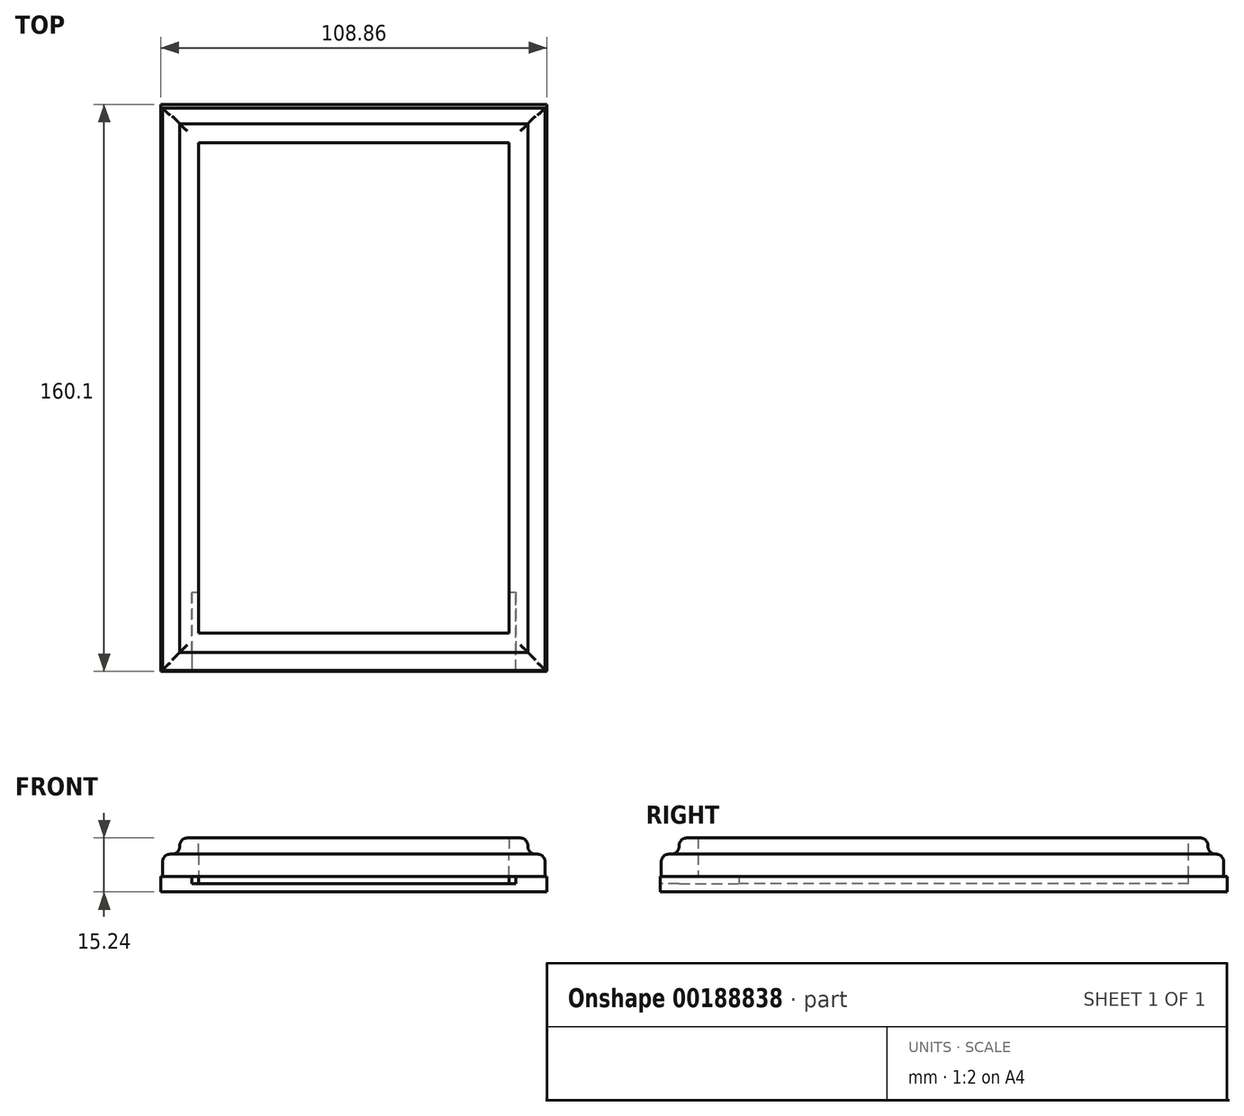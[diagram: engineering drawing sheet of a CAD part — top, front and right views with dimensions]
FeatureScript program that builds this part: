
annotation { "Feature Type Name" : "Feature", "Feature Type Description" : "" }
export const myFeature = defineFeature(function(context is Context, id is Id, definition is map)
    precondition{}
    {
        {
            var Q0;
            Q0=qCreatedBy(makeId("Top.planeOp"),FACE);
            var sketch = newSketch(context, id + "F0", { "sketchPlane" : qUnion([Q0])});
            skLineSegment(sketch, "E0.bottom", {"start": v(-90.68, 102.35) * mm, "end": v(17.27, 102.35) * mm});
            skLineSegment(sketch, "E0.top", {"start": v(-90.68, -56.4) * mm, "end": v(17.27, -56.4) * mm});
            skLineSegment(sketch, "E0.left", {"start": v(-90.68, 102.35) * mm, "end": v(-90.68, -56.4) * mm});
            skLineSegment(sketch, "E0.right", {"start": v(17.27, 102.35) * mm, "end": v(17.27, -56.4) * mm});
            skLineSegment(sketch, "E1.bottom", {"start": v(-90.68, 102.35) * mm, "end": v(-82.04, 102.35) * mm});
            skLineSegment(sketch, "E1.left", {"start": v(-90.68, 102.35) * mm, "end": v(-90.68, 93.72) * mm});
            skLineSegment(sketch, "E2.bottom", {"start": v(17.27, 102.35) * mm, "end": v(8.64, 102.35) * mm});
            skLineSegment(sketch, "E2.left", {"start": v(17.27, 102.35) * mm, "end": v(17.27, 93.72) * mm});
            skLineSegment(sketch, "E3.bottom", {"start": v(-90.68, -56.4) * mm, "end": v(-82.04, -56.4) * mm});
            skLineSegment(sketch, "E3.left", {"start": v(-90.68, -56.4) * mm, "end": v(-90.68, -47.76) * mm});
            skLineSegment(sketch, "E4.bottom", {"start": v(17.27, -56.4) * mm, "end": v(8.64, -56.4) * mm});
            skLineSegment(sketch, "E4.left", {"start": v(17.27, -56.4) * mm, "end": v(17.27, -47.76) * mm});
            skLineSegment(sketch, "E5.bottom", {"start": v(-80.54, 92.48) * mm, "end": v(7.1, 92.48) * mm});
            skLineSegment(sketch, "E5.top", {"start": v(-80.54, -45.95) * mm, "end": v(7.1, -45.95) * mm});
            skLineSegment(sketch, "E5.left", {"start": v(-80.54, 92.48) * mm, "end": v(-80.54, -45.95) * mm});
            skLineSegment(sketch, "E5.right", {"start": v(7.1, 92.48) * mm, "end": v(7.1, -45.95) * mm});
            skPoint(sketch, "E3.right.end.orphan", {"position": v(-80.54, -45.95) * mm});
            skSolve(sketch);
        }
        {
            var Q0;
            Q0 = qSketchRegion(id + "F0", true);
            extrude(context, id + "F1", {"entities" : qUnion([Q0]), "depth" : 6.35 * mm});
        }
        {
            var Q0;
            Q0=qCreatedBy(makeId("Top.planeOp"),FACE);
            var sketch = newSketch(context, id + "F2", { "sketchPlane" : qUnion([Q0])});
            skLineSegment(sketch, "E6.bottom", {"start": v(-91.13, -56.74) * mm, "end": v(-82.42, -56.74) * mm});
            skLineSegment(sketch, "E6.top", {"start": v(-91.13, 103.36) * mm, "end": v(17.73, 103.36) * mm});
            skLineSegment(sketch, "E6.left", {"start": v(-91.13, -56.74) * mm, "end": v(-91.13, 103.36) * mm});
            skLineSegment(sketch, "E6.right", {"start": v(17.73, -56.74) * mm, "end": v(17.73, 103.36) * mm});
            skLineSegment(sketch, "E7.top", {"start": v(-82.42, 94.23) * mm, "end": v(9.02, 94.23) * mm});
            skLineSegment(sketch, "E7.left", {"start": v(-82.42, -48.01) * mm, "end": v(-82.42, 94.23) * mm});
            skLineSegment(sketch, "E7.right", {"start": v(9.02, -48.01) * mm, "end": v(9.02, 94.23) * mm});
            skLineSegment(sketch, "E8", {"start": v(44.34, -69.5) * mm, "end": v(109.88, 53.73) * mm});
            skLineSegment(sketch, "E9", {"start": v(9.02, -48.01) * mm, "end": v(9.02, -56.74) * mm});
            skLineSegment(sketch, "E10", {"start": v(9.02, -56.74) * mm, "end": v(9.02, -48.01) * mm});
            skLineSegment(sketch, "E11", {"start": v(-82.42, -48.01) * mm, "end": v(-82.42, -56.74) * mm});
            skLineSegment(sketch, "E12", {"start": v(-82.42, -56.74) * mm, "end": v(-82.42, -48.01) * mm});
            skLineSegment(sketch, "E13.trimOffspring", {"start": v(9.02, -56.74) * mm, "end": v(17.73, -56.74) * mm});
            skSolve(sketch);
        }
        {
            var Q0;
            Q0=makeQuery(id+"F2.imprint","IMPRINT",FACE,{"disambiguationData":[TD([[makeQuery(id+"F2.imprint","IMPRINT",EDGE,{"derivedFrom":sQuery(id+"F2.wireOp",EDGE,"E6.bottom")}),1.0]])]});
            extrude(context, id + "F3", {"entities" : qUnion([Q0]), "operationType" : NewBodyOperationType.ADD, "oppositeDirection" : true, "depth" : 2.03 * mm});
        }
        {
            var Q0;
            Q0=qCreatedBy(makeId("Top.planeOp"),FACE);
            cPlane(context, id + "F4", {"entities" : qUnion([Q0]), "cplaneType" : CPlaneType.OFFSET, "offset" : 2.03 * mm, "oppositeDirection" : true, "width" : 152.4 * mm, "height" : 152.4 * mm});
        }
        {
            var Q0;
            Q0=qCreatedBy(id+"F4.planeOp",FACE);
            var sketch = newSketch(context, id + "F5", { "sketchPlane" : qUnion([Q0])});
            skLineSegment(sketch, "E14.bottom", {"start": v(-91.13, -56.74) * mm, "end": v(17.73, -56.74) * mm});
            skLineSegment(sketch, "E14.top", {"start": v(-91.13, 103.36) * mm, "end": v(17.73, 103.36) * mm});
            skLineSegment(sketch, "E14.left", {"start": v(-91.13, -56.74) * mm, "end": v(-91.13, 103.36) * mm});
            skLineSegment(sketch, "E14.right", {"start": v(17.73, -56.74) * mm, "end": v(17.73, 103.36) * mm});
            skSolve(sketch);
        }
        {
            var Q0;
            Q0 = qSketchRegion(id + "F5", true);
            extrude(context, id + "F6", {"entities" : qUnion([Q0]), "operationType" : NewBodyOperationType.ADD, "oppositeDirection" : true, "depth" : 2.3 * mm});
        }
        {
            var Q0;
            Q0=qCreatedBy(makeId("Top.planeOp"),FACE);
            var sketch = newSketch(context, id + "F7", { "sketchPlane" : qUnion([Q0])});
            skLineSegment(sketch, "E15.bottom", {"start": v(-80.54, 92.48) * mm, "end": v(7.1, 92.48) * mm});
            skLineSegment(sketch, "E15.top", {"start": v(-80.54, -45.95) * mm, "end": v(7.1, -45.95) * mm});
            skLineSegment(sketch, "E15.left", {"start": v(-80.54, 92.48) * mm, "end": v(-80.54, -45.95) * mm});
            skLineSegment(sketch, "E15.right", {"start": v(7.1, 92.48) * mm, "end": v(7.1, -45.95) * mm});
            skLineSegment(sketch, "E16.left", {"start": v(7.1, -45.95) * mm, "end": v(7.1, -51.34) * mm});
            skPoint(sketch, "E17.firstSnap0", {"position": v(-85.84, 92.48) * mm});
            skPoint(sketch, "E17.firstSnap1", {"position": v(-80.54, 97.92) * mm});
            skPoint(sketch, "E17.oppositeSnap0", {"position": v(17.73, -51.34) * mm});
            skPoint(sketch, "E17.oppositeSnap1", {"position": v(12.41, -45.95) * mm});
            skLineSegment(sketch, "E17.bottom", {"start": v(-85.84, 97.92) * mm, "end": v(12.41, 97.92) * mm});
            skLineSegment(sketch, "E17.top", {"start": v(-85.84, -51.34) * mm, "end": v(12.41, -51.34) * mm});
            skLineSegment(sketch, "E17.left", {"start": v(-85.84, 97.92) * mm, "end": v(-85.84, -51.34) * mm});
            skLineSegment(sketch, "E17.right", {"start": v(12.41, 97.92) * mm, "end": v(12.41, -51.34) * mm});
            skPoint(sketch, "E18.orphan", {"position": v(17.73, -56.74) * mm});
            skPoint(sketch, "E16.right.start.orphan", {"position": v(17.73, -45.95) * mm});
            skPoint(sketch, "E19.top.start.orphan", {"position": v(-80.54, 103.36) * mm});
            skPoint(sketch, "E19.right.start.orphan", {"position": v(-91.13, 92.48) * mm});
            skSolve(sketch);
        }
        {
            var Q0;
            Q0 = qSketchRegion(id + "F7", true);
            extrude(context, id + "F8", {"entities" : qUnion([Q0]), "operationType" : NewBodyOperationType.ADD, "oppositeDirection" : true, "depth" : 4.2 * mm});
        }
        {
            var Q0;
            Q0=qCreatedBy(makeId("Top.planeOp"),FACE);
            var sketch = newSketch(context, id + "F9", { "sketchPlane" : qUnion([Q0])});
            skLineSegment(sketch, "E20.bottom", {"start": v(-80.54, 92.48) * mm, "end": v(7.1, 92.48) * mm});
            skLineSegment(sketch, "E20.top", {"start": v(-80.54, -45.95) * mm, "end": v(7.1, -45.95) * mm});
            skLineSegment(sketch, "E20.left", {"start": v(-80.54, 92.48) * mm, "end": v(-80.54, -45.95) * mm});
            skLineSegment(sketch, "E20.right", {"start": v(7.1, 92.48) * mm, "end": v(7.1, -45.95) * mm});
            skPoint(sketch, "E21.firstSnap0", {"position": v(-85.83, 103.35) * mm});
            skPoint(sketch, "E21.firstSnap1", {"position": v(-91.12, 97.91) * mm});
            skPoint(sketch, "E21.oppositeSnap0", {"position": v(7.1, -51.37) * mm});
            skPoint(sketch, "E21.oppositeSnap1", {"position": v(12.43, -45.95) * mm});
            skLineSegment(sketch, "E21.bottom", {"start": v(-85.83, 97.91) * mm, "end": v(12.43, 97.91) * mm});
            skLineSegment(sketch, "E21.top", {"start": v(-85.83, -51.37) * mm, "end": v(12.43, -51.37) * mm});
            skLineSegment(sketch, "E21.left", {"start": v(-85.83, 97.91) * mm, "end": v(-85.83, -51.37) * mm});
            skLineSegment(sketch, "E21.right", {"start": v(12.43, 97.91) * mm, "end": v(12.43, -51.37) * mm});
            skPoint(sketch, "E22.right.start.orphan", {"position": v(17.78, -45.95) * mm});
            skPoint(sketch, "E22.top.start.orphan", {"position": v(7.1, -56.78) * mm});
            skPoint(sketch, "E23.orphan", {"position": v(-91.12, 92.48) * mm});
            skPoint(sketch, "E24.orphan", {"position": v(-91.12, 103.35) * mm});
            skPoint(sketch, "E25.left.end.orphan", {"position": v(-80.54, 103.35) * mm});
            skSolve(sketch);
        }
        {
            var Q0;
            Q0 = qSketchRegion(id + "F9", true);
            extrude(context, id + "F10", {"entities" : qUnion([Q0]), "operationType" : NewBodyOperationType.ADD, "depth" : 10.92 * mm});
        }
        {
            var Q0;
            Q0=makeQuery(id+"F10.opExtrude","CAP_EDGE",EDGE,{"disambiguationData":[OSD([sQuery(id+"F9.wireOp",EDGE,"E21.right")])],"isStart":false});
            var Q1;
            Q1=makeQuery(id+"F10.boolean.opBoolean","INTERSECT",EDGE,{"derivedFrom":[makeQuery(id+"F1.opExtrude","CAP_FACE",FACE,{"disambiguationData":[OSD([sQuery(id+"F0.wireOp",EDGE,"E0.bottom"),sQuery(id+"F0.wireOp",EDGE,"E0.top"),sQuery(id+"F0.wireOp",EDGE,"E0.left"),sQuery(id+"F0.wireOp",EDGE,"E0.right"),sQuery(id+"F0.wireOp",EDGE,"E1.bottom"),sQuery(id+"F0.wireOp",EDGE,"E1.left"),sQuery(id+"F0.wireOp",EDGE,"E2.bottom"),sQuery(id+"F0.wireOp",EDGE,"E2.left"),sQuery(id+"F0.wireOp",EDGE,"E3.bottom"),sQuery(id+"F0.wireOp",EDGE,"E3.left"),sQuery(id+"F0.wireOp",EDGE,"E4.bottom"),sQuery(id+"F0.wireOp",EDGE,"E4.left"),sQuery(id+"F0.wireOp",EDGE,"E5.bottom"),sQuery(id+"F0.wireOp",EDGE,"E5.top"),sQuery(id+"F0.wireOp",EDGE,"E5.left"),sQuery(id+"F0.wireOp",EDGE,"E5.right")])],"isStart":false}),makeQuery(id+"F10.opExtrude","SWEPT_FACE",FACE,{"disambiguationData":[OSD([sQuery(id+"F9.wireOp",EDGE,"E21.right")])]})]});
            var Q2;
            Q2=makeQuery(id+"F1.opExtrude","CAP_EDGE",EDGE,{"disambiguationData":[OSD([sQuery(id+"F0.wireOp",EDGE,"E0.right"),sQuery(id+"F0.wireOp",EDGE,"E2.left"),sQuery(id+"F0.wireOp",EDGE,"E4.left")])],"isStart":false});
            var Q3;
            Q3=makeQuery(id+"F10.opExtrude","CAP_EDGE",EDGE,{"disambiguationData":[OSD([sQuery(id+"F9.wireOp",EDGE,"E21.bottom")])],"isStart":false});
            var Q4;
            Q4=makeQuery(id+"F10.boolean.opBoolean","INTERSECT",EDGE,{"derivedFrom":[makeQuery(id+"F1.opExtrude","CAP_FACE",FACE,{"disambiguationData":[OSD([sQuery(id+"F0.wireOp",EDGE,"E0.bottom"),sQuery(id+"F0.wireOp",EDGE,"E0.top"),sQuery(id+"F0.wireOp",EDGE,"E0.left"),sQuery(id+"F0.wireOp",EDGE,"E0.right"),sQuery(id+"F0.wireOp",EDGE,"E1.bottom"),sQuery(id+"F0.wireOp",EDGE,"E1.left"),sQuery(id+"F0.wireOp",EDGE,"E2.bottom"),sQuery(id+"F0.wireOp",EDGE,"E2.left"),sQuery(id+"F0.wireOp",EDGE,"E3.bottom"),sQuery(id+"F0.wireOp",EDGE,"E3.left"),sQuery(id+"F0.wireOp",EDGE,"E4.bottom"),sQuery(id+"F0.wireOp",EDGE,"E4.left"),sQuery(id+"F0.wireOp",EDGE,"E5.bottom"),sQuery(id+"F0.wireOp",EDGE,"E5.top"),sQuery(id+"F0.wireOp",EDGE,"E5.left"),sQuery(id+"F0.wireOp",EDGE,"E5.right")])],"isStart":false}),makeQuery(id+"F10.opExtrude","SWEPT_FACE",FACE,{"disambiguationData":[OSD([sQuery(id+"F9.wireOp",EDGE,"E21.bottom")])]})]});
            var Q5;
            Q5=makeQuery(id+"F1.opExtrude","CAP_EDGE",EDGE,{"disambiguationData":[OSD([sQuery(id+"F0.wireOp",EDGE,"E0.bottom"),sQuery(id+"F0.wireOp",EDGE,"E1.bottom"),sQuery(id+"F0.wireOp",EDGE,"E2.bottom")])],"isStart":false});
            var Q6;
            Q6=makeQuery(id+"F10.opExtrude","CAP_EDGE",EDGE,{"disambiguationData":[OSD([sQuery(id+"F9.wireOp",EDGE,"E21.left")])],"isStart":false});
            var Q7;
            Q7=makeQuery(id+"F1.opExtrude","CAP_EDGE",EDGE,{"disambiguationData":[OSD([sQuery(id+"F0.wireOp",EDGE,"E0.left"),sQuery(id+"F0.wireOp",EDGE,"E1.left"),sQuery(id+"F0.wireOp",EDGE,"E3.left")])],"isStart":false});
            var Q8;
            Q8=makeQuery(id+"F10.boolean.opBoolean","INTERSECT",EDGE,{"derivedFrom":[makeQuery(id+"F1.opExtrude","CAP_FACE",FACE,{"disambiguationData":[OSD([sQuery(id+"F0.wireOp",EDGE,"E0.bottom"),sQuery(id+"F0.wireOp",EDGE,"E0.top"),sQuery(id+"F0.wireOp",EDGE,"E0.left"),sQuery(id+"F0.wireOp",EDGE,"E0.right"),sQuery(id+"F0.wireOp",EDGE,"E1.bottom"),sQuery(id+"F0.wireOp",EDGE,"E1.left"),sQuery(id+"F0.wireOp",EDGE,"E2.bottom"),sQuery(id+"F0.wireOp",EDGE,"E2.left"),sQuery(id+"F0.wireOp",EDGE,"E3.bottom"),sQuery(id+"F0.wireOp",EDGE,"E3.left"),sQuery(id+"F0.wireOp",EDGE,"E4.bottom"),sQuery(id+"F0.wireOp",EDGE,"E4.left"),sQuery(id+"F0.wireOp",EDGE,"E5.bottom"),sQuery(id+"F0.wireOp",EDGE,"E5.top"),sQuery(id+"F0.wireOp",EDGE,"E5.left"),sQuery(id+"F0.wireOp",EDGE,"E5.right")])],"isStart":false}),makeQuery(id+"F10.opExtrude","SWEPT_FACE",FACE,{"disambiguationData":[OSD([sQuery(id+"F9.wireOp",EDGE,"E21.top")])]})]});
            var Q9;
            Q9=makeQuery(id+"F10.opExtrude","CAP_EDGE",EDGE,{"disambiguationData":[OSD([sQuery(id+"F9.wireOp",EDGE,"E21.top")])],"isStart":false});
            var Q10;
            Q10=makeQuery(id+"F1.opExtrude","CAP_EDGE",EDGE,{"disambiguationData":[OSD([sQuery(id+"F0.wireOp",EDGE,"E0.top"),sQuery(id+"F0.wireOp",EDGE,"E3.bottom"),sQuery(id+"F0.wireOp",EDGE,"E4.bottom")])],"isStart":false});
            var Q11;
            Q11=makeQuery(id+"F10.boolean.opBoolean","INTERSECT",EDGE,{"derivedFrom":[makeQuery(id+"F1.opExtrude","CAP_FACE",FACE,{"disambiguationData":[OSD([sQuery(id+"F0.wireOp",EDGE,"E0.bottom"),sQuery(id+"F0.wireOp",EDGE,"E0.top"),sQuery(id+"F0.wireOp",EDGE,"E0.left"),sQuery(id+"F0.wireOp",EDGE,"E0.right"),sQuery(id+"F0.wireOp",EDGE,"E1.bottom"),sQuery(id+"F0.wireOp",EDGE,"E1.left"),sQuery(id+"F0.wireOp",EDGE,"E2.bottom"),sQuery(id+"F0.wireOp",EDGE,"E2.left"),sQuery(id+"F0.wireOp",EDGE,"E3.bottom"),sQuery(id+"F0.wireOp",EDGE,"E3.left"),sQuery(id+"F0.wireOp",EDGE,"E4.bottom"),sQuery(id+"F0.wireOp",EDGE,"E4.left"),sQuery(id+"F0.wireOp",EDGE,"E5.bottom"),sQuery(id+"F0.wireOp",EDGE,"E5.top"),sQuery(id+"F0.wireOp",EDGE,"E5.left"),sQuery(id+"F0.wireOp",EDGE,"E5.right")])],"isStart":false}),makeQuery(id+"F10.opExtrude","SWEPT_FACE",FACE,{"disambiguationData":[OSD([sQuery(id+"F9.wireOp",EDGE,"E21.left")])]})]});
            fillet(context, id + "F11", {"entities" : qUnion([Q0, Q1, Q2, Q3, Q4, Q5, Q6, Q7, Q8, Q9, Q10, Q11]), "radius" : 2.15 * mm, "tangentPropagation" : true, "allowEdgeOverflow" : false});
        }
        {
            var Q0;
            Q0=makeQuery(id+"F6.opExtrude","SWEPT_FACE",FACE,{"disambiguationData":[OSD([sQuery(id+"F5.wireOp",EDGE,"E14.bottom")])]});
            var sketch = newSketch(context, id + "F12", { "sketchPlane" : qUnion([Q0])});
            skLineSegment(sketch, "E26", {"start": v(-82.42, -2.03) * mm, "end": v(-82.42, 0) * mm});
            skLineSegment(sketch, "E27", {"start": v(-82.42, 0) * mm, "end": v(9.02, 0) * mm});
            skLineSegment(sketch, "E28", {"start": v(9.02, 0) * mm, "end": v(9.02, -2.03) * mm});
            skLineSegment(sketch, "E29", {"start": v(9.02, -2.03) * mm, "end": v(-82.42, -2.03) * mm});
            skSolve(sketch);
        }
        {
            var Q0;
            Q0 = qSketchRegion(id + "F12", true);
            extrude(context, id + "F13", {"entities" : qUnion([Q0]), "operationType" : NewBodyOperationType.REMOVE, "oppositeDirection" : true, "depth" : 22.35 * mm});
        }
    });
